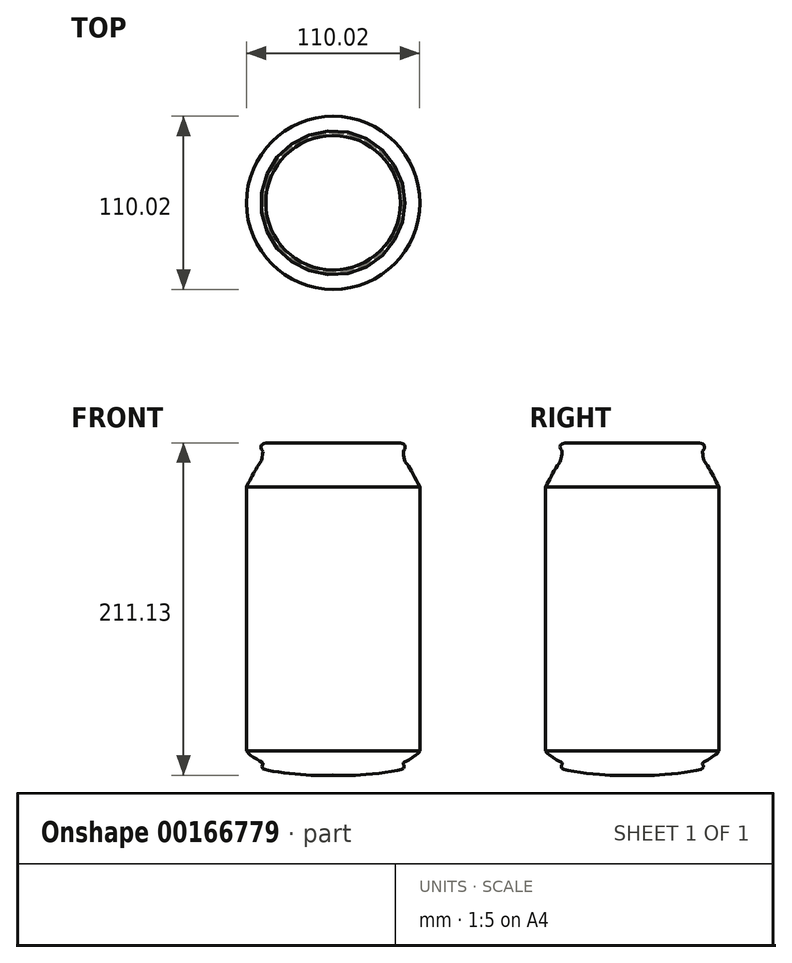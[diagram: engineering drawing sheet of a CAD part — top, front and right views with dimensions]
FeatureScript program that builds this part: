
annotation { "Feature Type Name" : "Feature", "Feature Type Description" : "" }
export const myFeature = defineFeature(function(context is Context, id is Id, definition is map)
    precondition{}
    {
        {
            var Q0;
            Q0=qCreatedBy(makeId("Front.planeOp"),FACE);
            var sketch = newSketch(context, id + "F0", { "sketchPlane" : qUnion([Q0])});
            skFitSpline(sketch, "E0", {"points": [v(0, -141.57) * mm, v(-13.65, -142) * mm, v(-33.48, -140.1) * mm, v(-44.39, -137.9) * mm, v(-44.97, -137) * mm, v(-45.08, -135.62) * mm, v(-44.44, -134.67) * mm, v(-48.77, -131.72) * mm, v(-53.96, -127.99) * mm, v(-55.01, -126.49) * mm], "startDerivative": vector(-73.27, -4.88) * mm, "endDerivative": vector(-12.05, 21.73) * mm});
            skLineSegment(sketch, "E1", {"start": v(-55.01, -126.49) * mm, "end": v(-55.01, 41.16) * mm});
            skFitSpline(sketch, "E2", {"points": [v(-55.01, 41.16) * mm, v(-50.1, 50.56) * mm, v(-46.96, 55.7) * mm, v(-45.63, 57.61) * mm, v(-44.79, 61.6) * mm, v(-44.79, 64.27) * mm, v(-45.58, 65.34) * mm, v(-45.66, 67.35) * mm, v(-44.68, 68.42) * mm, v(-42.73, 69.1) * mm], "startDerivative": vector(24.87, 48.76) * mm, "endDerivative": vector(23.5, 6.62) * mm});
            skLineSegment(sketch, "E3", {"start": v(-42.73, 69.1) * mm, "end": v(0, 69.1) * mm});
            skLineSegment(sketch, "E4", {"start": v(0, 69.1) * mm, "end": v(0, -141.57) * mm});
            skSolve(sketch);
        }
        {
            var Q0;
            Q0=makeQuery(id+"F0.imprint","IMPRINT",FACE,{"disambiguationData":[TD([[makeQuery(id+"F0.imprint","IMPRINT",EDGE,{"derivedFrom":sQuery(id+"F0.wireOp",EDGE,"E0")}),-1.0]])]});
            var Q1;
            Q1=sQuery(id+"F0.wireOp",EDGE,"E4");
            revolve(context, id + "F1", {"entities" : qUnion([Q0]), "axis" : qUnion([Q1]), "revolveType" : RevolveType.FULL});
        }
    });
